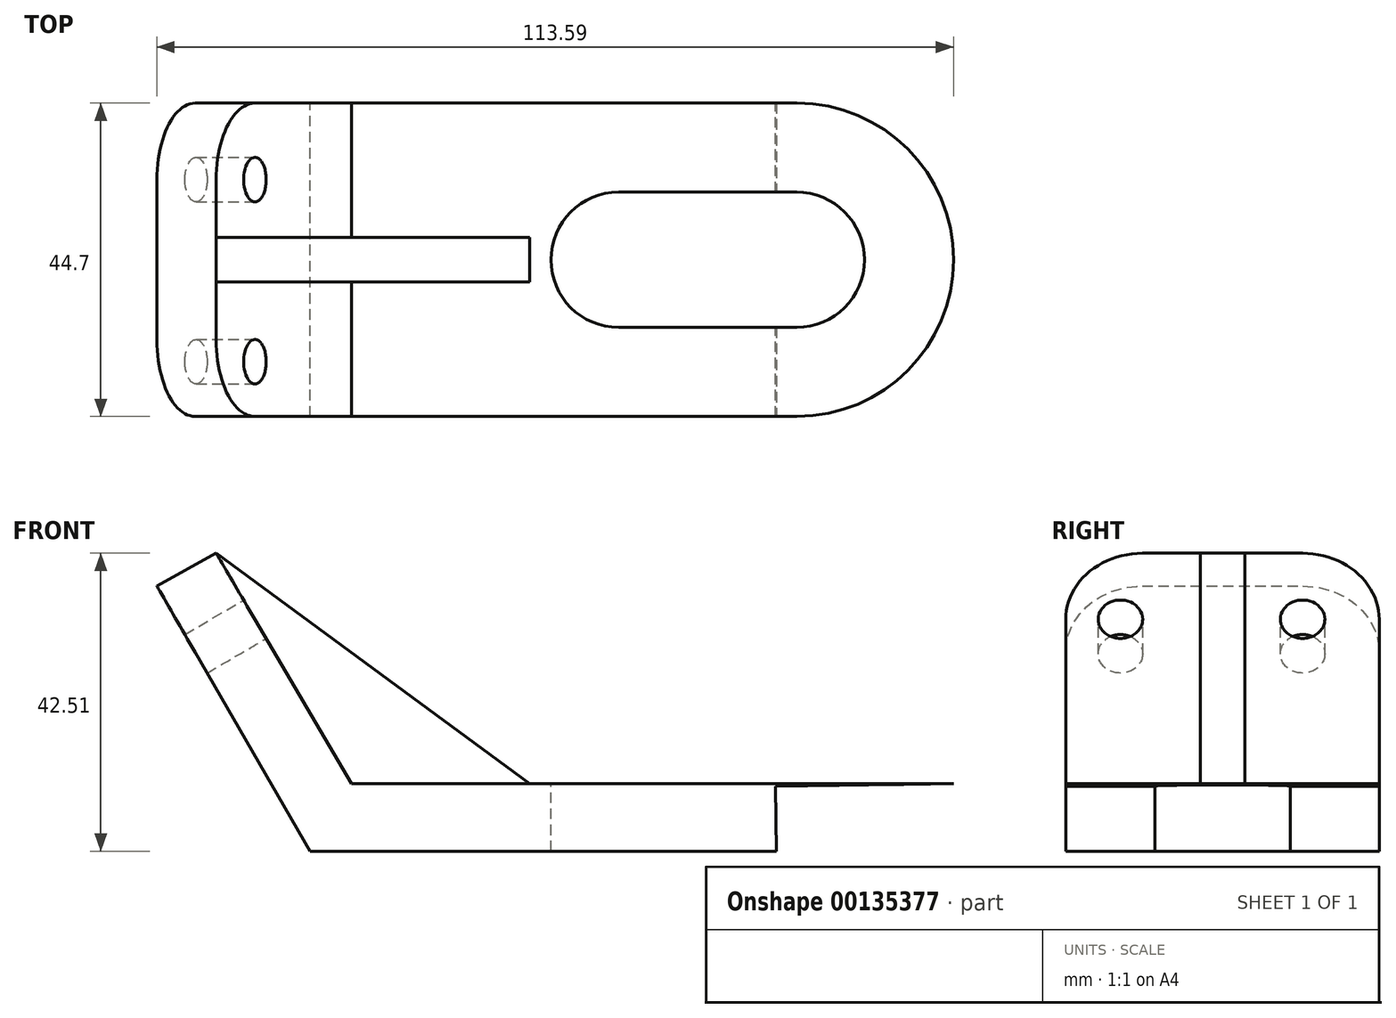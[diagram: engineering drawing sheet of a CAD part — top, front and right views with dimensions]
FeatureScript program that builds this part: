
annotation { "Feature Type Name" : "Feature", "Feature Type Description" : "" }
export const myFeature = defineFeature(function(context is Context, id is Id, definition is map)
    precondition{}
    {
        {
            var Q0;
            Q0=qCreatedBy(makeId("Front.planeOp"),FACE);
            var sketch = newSketch(context, id + "F0", { "sketchPlane" : qUnion([Q0])});
            skLineSegment(sketch, "E0", {"start": v(0, 0) * mm, "end": v(85.85, 0) * mm});
            skLineSegment(sketch, "E1", {"start": v(0, 0) * mm, "end": v(-19.29, 32.86) * mm});
            skLineSegment(sketch, "E2", {"start": v(85.85, 0) * mm, "end": v(86, -9.65) * mm});
            skLineSegment(sketch, "E3", {"start": v(86, -9.65) * mm, "end": v(-5.9, -9.65) * mm});
            skLineSegment(sketch, "E4", {"start": v(-5.9, -9.65) * mm, "end": v(-27.74, 28.18) * mm});
            skLineSegment(sketch, "E5", {"start": v(-27.74, 28.18) * mm, "end": v(-19.29, 32.86) * mm});
            skSolve(sketch);
        }
        {
            var Q0;
            Q0 = qSketchRegion(id + "F0", true);
            extrude(context, id + "F1", {"entities" : qUnion([Q0]), "endBound" : BoundingType.SYMMETRIC, "depth" : 44.7 * mm});
        }
        {
            var Q0;
            Q0=makeQuery(id+"F1.opExtrude","SWEPT_FACE",FACE,{"disambiguationData":[OSD([sQuery(id+"F0.wireOp",EDGE,"E0")])]});
            var sketch = newSketch(context, id + "F2", { "sketchPlane" : qUnion([Q0])});
            skLineSegment(sketch, "E6", {"start": v(38.1, 9.65) * mm, "end": v(63.5, 9.65) * mm});
            skLineSegment(sketch, "E7", {"start": v(38.1, -9.65) * mm, "end": v(63.5, -9.65) * mm});
            skArc(sketch, "E8", {"start": v(63.5, -9.65) * mm, "mid": v(73.15, 0) * mm, "end": v(63.5, 9.65) * mm});
            skArc(sketch, "E9", {"start": v(38.1, 9.65) * mm, "mid": v(28.45, 0) * mm, "end": v(38.1, -9.65) * mm});
            skArc(sketch, "E10.0", {"start": v(63.5, -22.35) * mm, "mid": v(85.85, 0) * mm, "end": v(63.5, 22.35) * mm});
            skLineSegment(sketch, "E11.0", {"start": v(0, 22.35) * mm, "end": v(85.85, 22.35) * mm});
            skLineSegment(sketch, "E12.0", {"start": v(85.85, -22.35) * mm, "end": v(85.85, 22.35) * mm});
            skLineSegment(sketch, "E13.0", {"start": v(0, -22.35) * mm, "end": v(85.85, -22.35) * mm});
            skSolve(sketch);
        }
        {
            var Q0;
            Q0 = qSketchRegion(id + "F2", true);
            extrude(context, id + "F3", {"entities" : qUnion([Q0]), "operationType" : NewBodyOperationType.REMOVE, "oppositeDirection" : true, "depth" : 25.4 * mm});
        }
        {
            var Q0;
            Q0=makeQuery(id+"F1.opExtrude","SWEPT_FACE",FACE,{"disambiguationData":[OSD([sQuery(id+"F0.wireOp",EDGE,"E2")])]});
            extrude(context, id + "F4", {"entities" : qUnion([Q0]), "operationType" : NewBodyOperationType.REMOVE, "oppositeDirection" : true, "depth" : 25.4 * mm});
        }
        {
            var Q0;
            Q0=makeQuery(id+"F1.opExtrude","SWEPT_FACE",FACE,{"disambiguationData":[OSD([sQuery(id+"F0.wireOp",EDGE,"E1")])]});
            var sketch = newSketch(context, id + "F5", { "sketchPlane" : qUnion([Q0])});
            skCircle(sketch, "E14", {"center": v(11.43, 27.18) * mm, "radius": 3.18 * mm});
            skCircle(sketch, "E15", {"center": v(-14.55, 27.18) * mm, "radius": 3.18 * mm});
            skSolve(sketch);
        }
        {
            var Q0;
            Q0=makeQuery(id+"F5.imprint","IMPRINT",FACE,{"disambiguationData":[TD([[makeQuery(id+"F5.imprint","IMPRINT",EDGE,{"derivedFrom":sQuery(id+"F5.wireOp",EDGE,"E14")}),1.0]])]});
            var Q1;
            Q1=makeQuery(id+"F5.imprint","IMPRINT",FACE,{"disambiguationData":[TD([[makeQuery(id+"F5.imprint","IMPRINT",EDGE,{"derivedFrom":sQuery(id+"F5.wireOp",EDGE,"E15")}),1.0]])]});
            extrude(context, id + "F6", {"entities" : qUnion([Q0, Q1]), "operationType" : NewBodyOperationType.REMOVE, "oppositeDirection" : true, "depth" : 25.4 * mm});
        }
        {
            var Q0;
            Q0=makeQuery(id+"F1.opExtrude","CAP_EDGE",EDGE,{"disambiguationData":[OSD([sQuery(id+"F0.wireOp",EDGE,"E5")])],"isStart":true});
            var Q1;
            Q1=makeQuery(id+"F1.opExtrude","CAP_EDGE",EDGE,{"disambiguationData":[OSD([sQuery(id+"F0.wireOp",EDGE,"E5")])],"isStart":false});
            fillet(context, id + "F7", {"entities" : qUnion([Q0, Q1]), "radius" : 10.92 * mm, "tangentPropagation" : true, "allowEdgeOverflow" : false});
        }
        {
            var Q0;
            Q0=qCreatedBy(makeId("Front.planeOp"),FACE);
            var sketch = newSketch(context, id + "F8", { "sketchPlane" : qUnion([Q0])});
            skLineSegment(sketch, "E16.0", {"start": v(-19.29, 32.86) * mm, "end": v(-13.76, 23.43) * mm});
            skLineSegment(sketch, "E16.1", {"start": v(0, 0) * mm, "end": v(-13.76, 23.43) * mm});
            skLineSegment(sketch, "E16.2", {"start": v(0, 0) * mm, "end": v(63.5, 0) * mm});
            skLineSegment(sketch, "E17", {"start": v(-19.29, 32.86) * mm, "end": v(25.4, 0) * mm});
            skSolve(sketch);
        }
        {
            var Q0;
            Q0 = qSketchRegion(id + "F8", true);
            extrude(context, id + "F9", {"entities" : qUnion([Q0]), "operationType" : NewBodyOperationType.ADD, "endBound" : BoundingType.SYMMETRIC, "depth" : 6.35 * mm});
        }
    });
